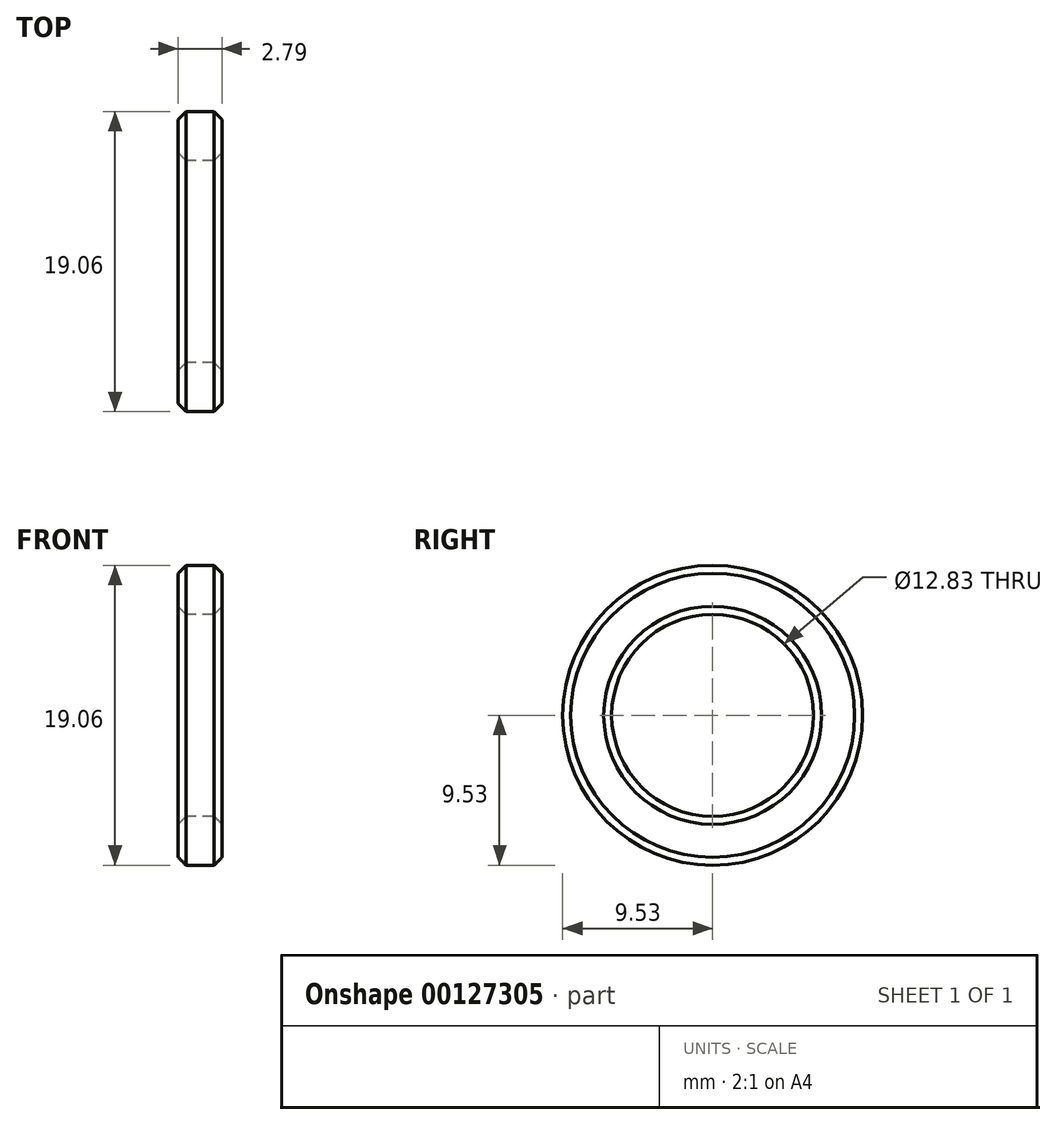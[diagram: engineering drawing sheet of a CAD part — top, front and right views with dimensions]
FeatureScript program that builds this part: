
annotation { "Feature Type Name" : "Feature", "Feature Type Description" : "" }
export const myFeature = defineFeature(function(context is Context, id is Id, definition is map)
    precondition{}
    {
        {
            var Q0;
            Q0=qCreatedBy(makeId("Right.planeOp"),FACE);
            var sketch = newSketch(context, id + "F0", { "sketchPlane" : qUnion([Q0])});
            skCircle(sketch, "E0", {"center": v(0, 0) * mm, "radius": 9.53 * mm});
            skCircle(sketch, "E1", {"center": v(0, 0) * mm, "radius": 6.41 * mm});
            skSolve(sketch);
        }
        {
            var Q0;
            Q0 = qSketchRegion(id + "F0", true);
            extrude(context, id + "F1", {"entities" : qUnion([Q0]), "depth" : 2.8 * mm});
        }
        {
            var Q0;
            Q0=makeQuery(id+"F1.opExtrude","SWEPT_FACE",FACE,{"disambiguationData":[OSD([sQuery(id+"F0.wireOp",EDGE,"E1")])]});
            var Q1;
            Q1=makeQuery(id+"F1.opExtrude","SWEPT_FACE",FACE,{"disambiguationData":[OSD([sQuery(id+"F0.wireOp",EDGE,"E0")])]});
            chamfer(context, id + "F2", {"entities" : qUnion([Q0, Q1]), "width" : 0.5 * mm, "tangentPropagation" : true});
        }
    });
